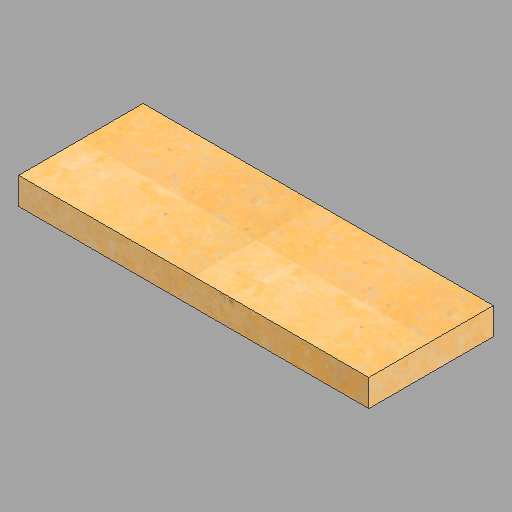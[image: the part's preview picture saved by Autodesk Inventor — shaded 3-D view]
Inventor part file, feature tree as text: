
AUTODESK INVENTOR PART (.ipt)
format: ipt  version: 2023 (Build 270158030, 158C)  size: 227,840 bytes
history: native  units: in
note: dims shown in document units (in); Inventor stores cm internally (conversion verified against a paired STEP export)
features: extrude x1, sketch x1
ambient origin geometry x8: Origin, YZ Plane, XZ Plane, XY Plane, X Axis, Y Axis, Z Axis, Center Point
bodies: Solid1 (feature_tree)
feature tree (2):
  extrude  "Extrusion1"  Depth=18.5in
  sketch  "Sketch1"  dims[d0=52.0in d1=18.5in d2=4.0in d3=0.0in]
